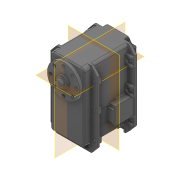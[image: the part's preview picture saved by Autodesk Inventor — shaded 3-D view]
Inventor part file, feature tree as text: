
AUTODESK INVENTOR PART (.ipt)
format: ipt  version: 2023.2 (Build 272271000, 271)  size: 397,312 bytes
history: native  units: mm
features: other x5, extrude x1, sketch x1, projected_geometry x1
ambient origin geometry x8: Origin, YZ Plane, XZ Plane, XY Plane, X Axis, Y Axis, Z Axis, Center Point
bodies: Body1 (feature_tree)
feature tree (8):
  other  "솔리드1"
  extrude  "돌출1"  Depth=2.5mm
  other  "작업 평면1"
  other  "작업 평면2"
  other  "작업 평면3"
  sketch  "스케치1"
  projected_geometry  "투영된 루프1"
  other  "기준1"
